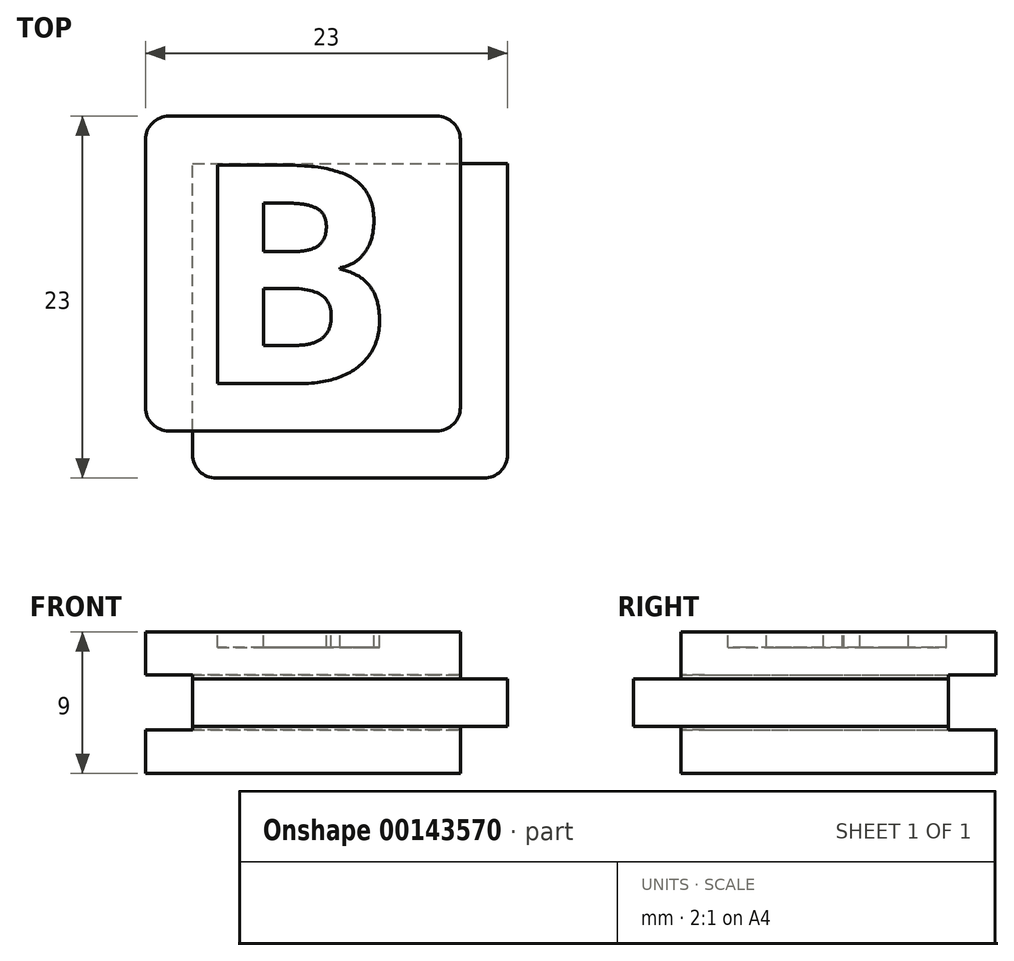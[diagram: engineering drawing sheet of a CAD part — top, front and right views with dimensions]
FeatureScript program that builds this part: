
annotation { "Feature Type Name" : "Feature", "Feature Type Description" : "" }
export const myFeature = defineFeature(function(context is Context, id is Id, definition is map)
    precondition{}
    {
        {
            var Q0;
            Q0=qCreatedBy(makeId("Front.planeOp"),FACE);
            var sketch = newSketch(context, id + "F0", { "sketchPlane" : qUnion([Q0])});
            skLineSegment(sketch, "E0.bottom", {"start": v(10, 4.5) * mm, "end": v(-10, 4.5) * mm});
            skLineSegment(sketch, "E0.top", {"start": v(10, -4.5) * mm, "end": v(-10, -4.5) * mm});
            skLineSegment(sketch, "E0.left", {"start": v(10, 4.5) * mm, "end": v(10, -4.5) * mm});
            skLineSegment(sketch, "E0.right", {"start": v(-10, 4.5) * mm, "end": v(-10, -4.5) * mm});
            skPoint(sketch, "E0.middle", {"position": v(0, 0) * mm});
            skLineSegment(sketch, "E1.bottom", {"start": v(13, 1.5) * mm, "end": v(7, 1.5) * mm});
            skLineSegment(sketch, "E1.top", {"start": v(13, -1.5) * mm, "end": v(7, -1.5) * mm});
            skLineSegment(sketch, "E1.left", {"start": v(13, 1.5) * mm, "end": v(13, -1.5) * mm});
            skLineSegment(sketch, "E1.right", {"start": v(7, 1.5) * mm, "end": v(7, -1.5) * mm});
            skPoint(sketch, "E1.middle", {"position": v(10, 0) * mm});
            skLineSegment(sketch, "E2.bottom", {"start": v(7, 1.5) * mm, "end": v(-7, 1.5) * mm});
            skLineSegment(sketch, "E2.top", {"start": v(7, -1.5) * mm, "end": v(-7, -1.5) * mm});
            skLineSegment(sketch, "E2.right", {"start": v(-7, 1.5) * mm, "end": v(-7, -1.5) * mm});
            skLineSegment(sketch, "E3.bottom", {"start": v(-7, -1.5) * mm, "end": v(-10, -1.5) * mm});
            skLineSegment(sketch, "E3.top", {"start": v(-7, 1.5) * mm, "end": v(-10, 1.5) * mm});
            skLineSegment(sketch, "E3.left", {"start": v(-7, -1.5) * mm, "end": v(-7, 1.5) * mm});
            skLineSegment(sketch, "E3.right", {"start": v(-10, -1.5) * mm, "end": v(-10, 1.5) * mm});
            skSolve(sketch);
        }
        {
            var Q0;
            {var subQ5=sQuery(id+"F0.wireOp",EDGE,"E0.bottom");Q0=makeQuery(id+"F0.imprint","IMPRINT",FACE,{"disambiguationData":[TD([[makeQuery(id+"F0.imprint","IMPRINT",EDGE,{"derivedFrom":subQ5}),1.0]])]});}
            var Q1;
            Q1=makeQuery(id+"F0.imprint","IMPRINT",FACE,{"disambiguationData":[TD([[makeQuery(id+"F0.imprint","IMPRINT",EDGE,{"derivedFrom":sQuery(id+"F0.wireOp",EDGE,"E2.bottom")}),1.0]])]});
            var Q2;
            {var subQ5=sQuery(id+"F0.wireOp",EDGE,"E1.left");Q2=makeQuery(id+"F0.imprint","IMPRINT",FACE,{"disambiguationData":[TD([[makeQuery(id+"F0.imprint","IMPRINT",EDGE,{"derivedFrom":subQ5}),-1.0]])]});}
            var Q3;
            {var subQ5=sQuery(id+"F0.wireOp",EDGE,"E1.right");Q3=makeQuery(id+"F0.imprint","IMPRINT",FACE,{"disambiguationData":[TD([[makeQuery(id+"F0.imprint","IMPRINT",EDGE,{"derivedFrom":subQ5}),1.0]])]});}
            var Q4;
            Q4=makeQuery(id+"F0.imprint","IMPRINT",FACE,{"disambiguationData":[TD([[makeQuery(id+"F0.imprint","IMPRINT",EDGE,{"derivedFrom":sQuery(id+"F0.wireOp",EDGE,"E3.bottom")}),-1.0]])]});
            var Q5;
            {var subQ5=sQuery(id+"F0.wireOp",EDGE,"E0.top");Q5=makeQuery(id+"F0.imprint","IMPRINT",FACE,{"disambiguationData":[TD([[makeQuery(id+"F0.imprint","IMPRINT",EDGE,{"derivedFrom":subQ5}),-1.0]])]});}
            extrude(context, id + "F1", {"entities" : qUnion([Q0, Q1, Q2, Q3, Q4, Q5]), "oppositeDirection" : true, "depth" : 20 * mm});
        }
        {
            var Q0;
            Q0=makeQuery(id+"F0.imprint","IMPRINT",FACE,{"disambiguationData":[TD([[makeQuery(id+"F0.imprint","IMPRINT",EDGE,{"derivedFrom":sQuery(id+"F0.wireOp",EDGE,"E3.bottom")}),-1.0]])]});
            var Q1;
            Q1=makeQuery(id+"F0.imprint","IMPRINT",FACE,{"disambiguationData":[TD([[makeQuery(id+"F0.imprint","IMPRINT",EDGE,{"derivedFrom":sQuery(id+"F0.wireOp",EDGE,"E2.bottom")}),1.0]])]});
            var Q2;
            {var subQ5=sQuery(id+"F0.wireOp",EDGE,"E1.right");Q2=makeQuery(id+"F0.imprint","IMPRINT",FACE,{"disambiguationData":[TD([[makeQuery(id+"F0.imprint","IMPRINT",EDGE,{"derivedFrom":subQ5}),1.0]])]});}
            var Q3;
            {var subQ5=sQuery(id+"F0.wireOp",EDGE,"E1.left");Q3=makeQuery(id+"F0.imprint","IMPRINT",FACE,{"disambiguationData":[TD([[makeQuery(id+"F0.imprint","IMPRINT",EDGE,{"derivedFrom":subQ5}),-1.0]])]});}
            extrude(context, id + "F2", {"entities" : qUnion([Q0, Q1, Q2, Q3]), "operationType" : NewBodyOperationType.ADD, "depth" : 3 * mm});
        }
        {
            var Q0;
            {var subQ0=sQuery(id+"F0.wireOp",EDGE,"E1.left");Q0=makeQuery(id+"F2.boolean.opBoolean","MERGE",FACE,{"derivedFrom":[makeQuery(id+"F1.opExtrude","SWEPT_FACE",FACE,{"disambiguationData":[OSD([subQ0])]}),makeQuery(id+"F2.opExtrude","SWEPT_FACE",FACE,{"disambiguationData":[OSD([subQ0])]})]});}
            var sketch = newSketch(context, id + "F3", { "sketchPlane" : qUnion([Q0])});
            skLineSegment(sketch, "E4.bottom", {"start": v(23, 1.75) * mm, "end": v(17, 1.75) * mm});
            skLineSegment(sketch, "E4.top", {"start": v(23, -1.75) * mm, "end": v(17, -1.75) * mm});
            skLineSegment(sketch, "E4.left", {"start": v(23, 1.75) * mm, "end": v(23, -1.75) * mm});
            skLineSegment(sketch, "E4.right", {"start": v(17, 1.75) * mm, "end": v(17, -1.75) * mm});
            skPoint(sketch, "E4.middle", {"position": v(20, 0) * mm});
            skSolve(sketch);
        }
        {
            var Q0;
            {var subQ1=sQuery(id+"F3.wireOp",EDGE,"E4.bottom");Q0=makeQuery(id+"F3.imprint","IMPRINT",FACE,{"disambiguationData":[TD([[makeQuery(id+"F3.imprint","IMPRINT",EDGE,{"derivedFrom":subQ1}),1.0]])]});}
            var Q1;
            {var subQ1=sQuery(id+"F0.wireOp",EDGE,"E1.left");var subQ8=makeQuery(id+"F1.opExtrude","CAP_EDGE",EDGE,{"disambiguationData":[OSD([subQ1])],"isStart":false});Q1=makeQuery(id+"F3.imprint","IMPRINT",FACE,{"disambiguationData":[TD([[makeQuery(id+"F3.imprint","IMPRINT",EDGE,{"derivedFrom":subQ8}),-1.0]])]});}
            extrude(context, id + "F4", {"entities" : qUnion([Q0, Q1]), "operationType" : NewBodyOperationType.REMOVE, "oppositeDirection" : true, "depth" : 100 * mm});
        }
        {
            var Q0;
            Q0=makeQuery(id+"F4.boolean.opBoolean","COPY",FACE,{"derivedFrom":makeQuery(id+"F4.opExtrude","SWEPT_FACE",FACE,{"disambiguationData":[OSD([sQuery(id+"F3.wireOp",EDGE,"E4.right")])]})});
            var sketch = newSketch(context, id + "F5", { "sketchPlane" : qUnion([Q0])});
            skLineSegment(sketch, "E5.bottom", {"start": v(13, 1.75) * mm, "end": v(7, 1.75) * mm});
            skLineSegment(sketch, "E5.top", {"start": v(13, -1.75) * mm, "end": v(7, -1.75) * mm});
            skLineSegment(sketch, "E5.left", {"start": v(13, 1.75) * mm, "end": v(13, -1.75) * mm});
            skLineSegment(sketch, "E5.right", {"start": v(7, 1.75) * mm, "end": v(7, -1.75) * mm});
            skPoint(sketch, "E5.middle", {"position": v(10, 0) * mm});
            skSolve(sketch);
        }
        {
            var Q0;
            {var subQ3=sQuery(id+"F5.wireOp",EDGE,"E5.left");Q0=makeQuery(id+"F5.imprint","IMPRINT",FACE,{"disambiguationData":[TD([[makeQuery(id+"F5.imprint","IMPRINT",EDGE,{"derivedFrom":subQ3}),-1.0]])]});}
            var Q1;
            {var subQ4=sQuery(id+"F5.wireOp",EDGE,"E5.right");Q1=makeQuery(id+"F5.imprint","IMPRINT",FACE,{"disambiguationData":[TD([[makeQuery(id+"F5.imprint","IMPRINT",EDGE,{"derivedFrom":subQ4}),1.0]])]});}
            extrude(context, id + "F6", {"entities" : qUnion([Q0, Q1]), "operationType" : NewBodyOperationType.REMOVE, "oppositeDirection" : true, "depth" : 100 * mm});
        }
        {
            var Q0;
            Q0=makeQuery(id+"F6.boolean.opBoolean","INTERSECT",EDGE,{"derivedFrom":[makeQuery(id+"F2.opExtrude","CAP_FACE",FACE,{"disambiguationData":[OSD([sQuery(id+"F0.wireOp",EDGE,"E1.bottom"),sQuery(id+"F0.wireOp",EDGE,"E1.top"),sQuery(id+"F0.wireOp",EDGE,"E1.left"),sQuery(id+"F0.wireOp",EDGE,"E2.bottom"),sQuery(id+"F0.wireOp",EDGE,"E2.top"),sQuery(id+"F0.wireOp",EDGE,"E3.bottom"),sQuery(id+"F0.wireOp",EDGE,"E3.top"),sQuery(id+"F0.wireOp",EDGE,"E3.right")])],"isStart":false}),makeQuery(id+"F6.opExtrude","SWEPT_FACE",FACE,{"disambiguationData":[OSD([sQuery(id+"F5.wireOp",EDGE,"E5.right")])]})]});
            var Q1;
            Q1=makeQuery(id+"F2.opExtrude","CAP_EDGE",EDGE,{"disambiguationData":[OSD([sQuery(id+"F0.wireOp",EDGE,"E1.left")])],"isStart":false});
            var Q2;
            {var subQ0=sQuery(id+"F0.wireOp",EDGE,"E0.left");Q2=makeQuery(id+"F1.opExtrude","CAP_EDGE",EDGE,{"disambiguationData":[OSD([subQ0]),TDD([makeQuery(id+"F0.imprint","IMPRINT",EDGE,{"disambiguationData":[TD([[makeQuery(id+"F0.imprint","INTERSECT",VERTEX,{"derivedFrom":[sQuery(id+"F0.wireOp",EDGE,"E0.bottom"),subQ0]}),-1.0]])],"derivedFrom":subQ0})])],"isStart":true});}
            var Q3;
            {var subQ0=sQuery(id+"F0.wireOp",EDGE,"E0.left");Q3=makeQuery(id+"F1.opExtrude","CAP_EDGE",EDGE,{"disambiguationData":[OSD([subQ0]),TDD([makeQuery(id+"F0.imprint","IMPRINT",EDGE,{"disambiguationData":[TD([[makeQuery(id+"F0.imprint","INTERSECT",VERTEX,{"derivedFrom":[sQuery(id+"F0.wireOp",EDGE,"E0.top"),subQ0]}),1.0]])],"derivedFrom":subQ0})])],"isStart":true});}
            var Q4;
            {var subQ0=sQuery(id+"F0.wireOp",EDGE,"E3.right");var subQ1=sQuery(id+"F0.wireOp",EDGE,"E0.right");var subQ3=sQuery(id+"F0.wireOp",EDGE,"E0.top");Q4=makeQuery(id+"F2.boolean.opBoolean","SPLIT",EDGE,{"disambiguationData":[TD([makeQuery(id+"F1.opExtrude","SWEPT_FACE",FACE,{"disambiguationData":[OSD([subQ3])]})])],"derivedFrom":makeQuery(id+"F1.opExtrude","CAP_EDGE",EDGE,{"disambiguationData":[OSD([subQ1,subQ0])],"isStart":true})});}
            var Q5;
            {var subQ1=sQuery(id+"F0.wireOp",EDGE,"E3.right");var subQ2=sQuery(id+"F0.wireOp",EDGE,"E0.right");var subQ3=sQuery(id+"F0.wireOp",EDGE,"E0.bottom");Q5=makeQuery(id+"F2.boolean.opBoolean","SPLIT",EDGE,{"disambiguationData":[TD([makeQuery(id+"F1.opExtrude","SWEPT_FACE",FACE,{"disambiguationData":[OSD([subQ3])]})])],"derivedFrom":makeQuery(id+"F1.opExtrude","CAP_EDGE",EDGE,{"disambiguationData":[OSD([subQ2,subQ1])],"isStart":true})});}
            var Q6;
            Q6=makeQuery(id+"F6.boolean.opBoolean","COPY",EDGE,{"derivedFrom":makeQuery(id+"F6.opExtrude","CAP_EDGE",EDGE,{"disambiguationData":[OSD([sQuery(id+"F5.wireOp",EDGE,"E5.right")])],"isStart":true})});
            var Q7;
            {var subQ0=sQuery(id+"F0.wireOp",EDGE,"E3.right");var subQ1=sQuery(id+"F0.wireOp",EDGE,"E0.right");var subQ2=sQuery(id+"F0.wireOp",EDGE,"E0.bottom");Q7=makeQuery(id+"F4.boolean.opBoolean","SPLIT",EDGE,{"disambiguationData":[TD([makeQuery(id+"F1.opExtrude","SWEPT_FACE",FACE,{"disambiguationData":[OSD([subQ2])]})])],"derivedFrom":makeQuery(id+"F1.opExtrude","CAP_EDGE",EDGE,{"disambiguationData":[OSD([subQ1,subQ0])],"isStart":false})});}
            var Q8;
            {var subQ0=sQuery(id+"F0.wireOp",EDGE,"E3.right");var subQ1=sQuery(id+"F0.wireOp",EDGE,"E0.right");var subQ2=sQuery(id+"F0.wireOp",EDGE,"E0.top");Q8=makeQuery(id+"F4.boolean.opBoolean","SPLIT",EDGE,{"disambiguationData":[TD([makeQuery(id+"F1.opExtrude","SWEPT_FACE",FACE,{"disambiguationData":[OSD([subQ2])]})])],"derivedFrom":makeQuery(id+"F1.opExtrude","CAP_EDGE",EDGE,{"disambiguationData":[OSD([subQ1,subQ0])],"isStart":false})});}
            var Q9;
            Q9=makeQuery(id+"F4.boolean.opBoolean","COPY",EDGE,{"derivedFrom":makeQuery(id+"F4.opExtrude","CAP_EDGE",EDGE,{"disambiguationData":[OSD([sQuery(id+"F3.wireOp",EDGE,"E4.right")])],"isStart":true})});
            var Q10;
            {var subQ0=sQuery(id+"F0.wireOp",EDGE,"E0.left");Q10=makeQuery(id+"F1.opExtrude","CAP_EDGE",EDGE,{"disambiguationData":[OSD([subQ0]),TDD([makeQuery(id+"F0.imprint","IMPRINT",EDGE,{"disambiguationData":[TD([[makeQuery(id+"F0.imprint","INTERSECT",VERTEX,{"derivedFrom":[sQuery(id+"F0.wireOp",EDGE,"E0.bottom"),subQ0]}),-1.0]])],"derivedFrom":subQ0})])],"isStart":false});}
            var Q11;
            {var subQ0=sQuery(id+"F0.wireOp",EDGE,"E0.left");Q11=makeQuery(id+"F1.opExtrude","CAP_EDGE",EDGE,{"disambiguationData":[OSD([subQ0]),TDD([makeQuery(id+"F0.imprint","IMPRINT",EDGE,{"disambiguationData":[TD([[makeQuery(id+"F0.imprint","INTERSECT",VERTEX,{"derivedFrom":[sQuery(id+"F0.wireOp",EDGE,"E0.top"),subQ0]}),1.0]])],"derivedFrom":subQ0})])],"isStart":false});}
            fillet(context, id + "F7", {"entities" : qUnion([Q0, Q1, Q2, Q3, Q4, Q5, Q6, Q7, Q8, Q9, Q10, Q11]), "radius" : 1.5 * mm, "tangentPropagation" : true, "allowEdgeOverflow" : false});
        }
        {
            var Q0;
            Q0=makeQuery(id+"F1.opExtrude","SWEPT_FACE",FACE,{"disambiguationData":[OSD([sQuery(id+"F0.wireOp",EDGE,"E0.bottom")])]});
            var sketch = newSketch(context, id + "F8", { "sketchPlane" : qUnion([Q0])});
            skText(sketch, "E6", { "text": "B", "fontName": "OpenSans-Bold.ttf"});
            skLineSegment(sketch, "E7.0", {"start": v(10, 3) * mm, "end": v(-11.07, 3) * mm});
            const initialGuessF8  = {"E6": [-0.00718, 0.003, 1, 0, 0.014]};
            skSetInitialGuess(sketch, initialGuessF8);
            skSolve(sketch);
        }
        {
            var Q0;
            Q0=makeQuery(id+"F8.imprint","IMPRINT",FACE,{"disambiguationData":[TD([[makeQuery(id+"F8.imprint","IMPRINT",EDGE,{"derivedFrom":sQuery(id+"F8.wireOp",EDGE,"E6.sketch_text.stroke-0")}),-1.0]])]});
            extrude(context, id + "F9", {"entities" : qUnion([Q0]), "operationType" : NewBodyOperationType.REMOVE, "oppositeDirection" : true, "depth" : 1 * mm});
        }
    });
